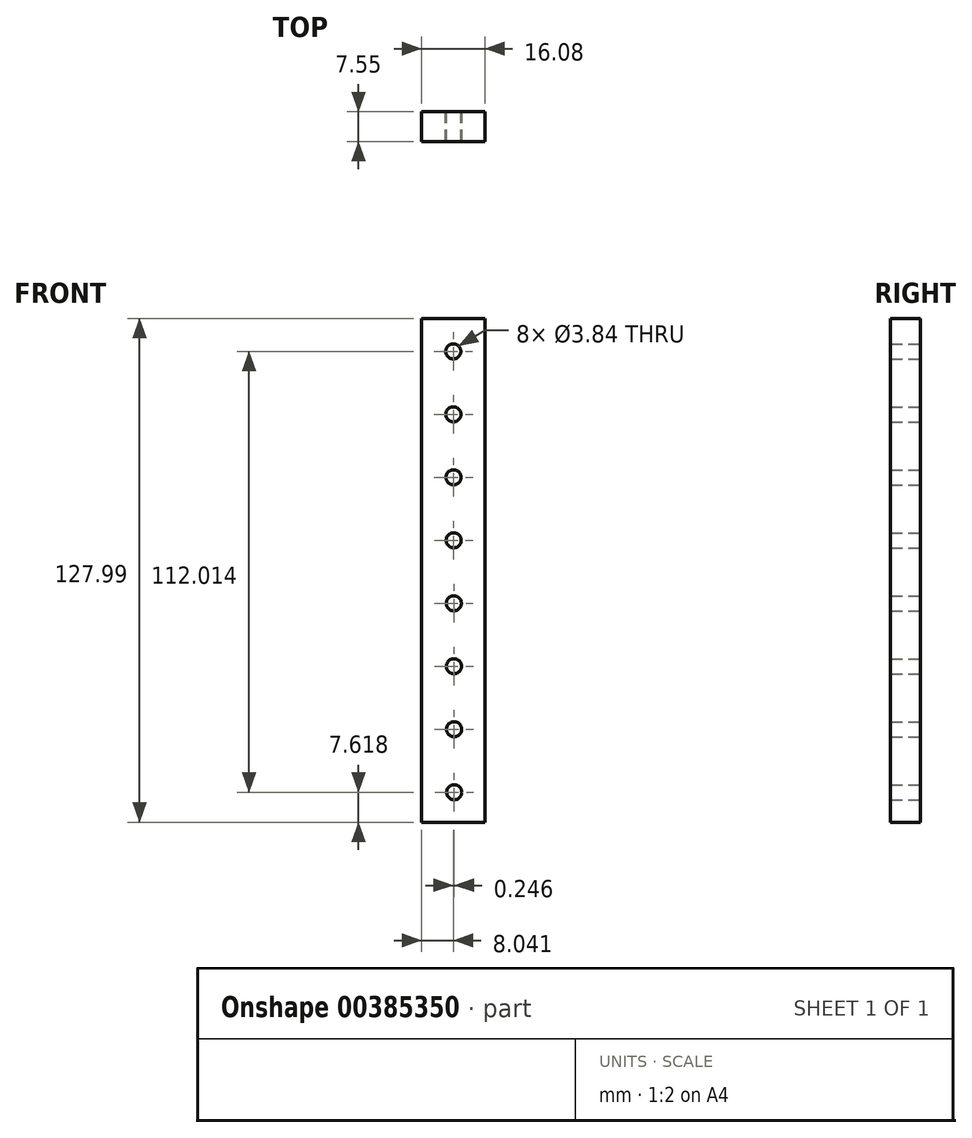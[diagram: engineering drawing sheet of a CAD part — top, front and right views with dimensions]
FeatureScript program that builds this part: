
annotation { "Feature Type Name" : "Feature", "Feature Type Description" : "" }
export const myFeature = defineFeature(function(context is Context, id is Id, definition is map)
    precondition{}
    {
        {
            var Q0;
            Q0=qCreatedBy(makeId("Front.planeOp"),FACE);
            var sketch = newSketch(context, id + "F0", { "sketchPlane" : qUnion([Q0])});
            skLineSegment(sketch, "E0", {"start": v(-32.66, 62.4) * mm, "end": v(-32.66, -65.58) * mm});
            skLineSegment(sketch, "E1", {"start": v(-32.66, -65.58) * mm, "end": v(-16.58, -65.58) * mm});
            skLineSegment(sketch, "E2", {"start": v(-32.66, 62.4) * mm, "end": v(-16.58, 62.4) * mm});
            skLineSegment(sketch, "E3", {"start": v(-16.58, 62.4) * mm, "end": v(-16.58, -65.58) * mm});
            skCircle(sketch, "E4", {"center": v(-24.62, 54.05) * mm, "radius": 1.92 * mm});
            skCircle(sketch, "E5.1.0.0", {"center": v(-24.58, 38.05) * mm, "radius": 1.92 * mm});
            skCircle(sketch, "E5.2.0.0", {"center": v(-24.55, 22.05) * mm, "radius": 1.92 * mm});
            skCircle(sketch, "E5.3.0.0", {"center": v(-24.51, 6.05) * mm, "radius": 1.92 * mm});
            skCircle(sketch, "E5.4.0.0", {"center": v(-24.48, -9.96) * mm, "radius": 1.92 * mm});
            skCircle(sketch, "E5.5.0.0", {"center": v(-24.44, -25.96) * mm, "radius": 1.92 * mm});
            skCircle(sketch, "E5.6.0.0", {"center": v(-24.4, -41.96) * mm, "radius": 1.92 * mm});
            skCircle(sketch, "E5.7.0.0", {"center": v(-24.37, -57.96) * mm, "radius": 1.92 * mm});
            skLineSegment(sketch, "E6", {"start": v(-16.58, 59.8) * mm, "end": v(-32.66, 59.8) * mm});
            skLineSegment(sketch, "E7.1.0.0", {"start": v(-16.58, 57.26) * mm, "end": v(-32.66, 57.26) * mm});
            skLineSegment(sketch, "E7.2.0.0", {"start": v(-16.58, 54.72) * mm, "end": v(-32.66, 54.72) * mm});
            skLineSegment(sketch, "E7.3.0.0", {"start": v(-16.58, 52.18) * mm, "end": v(-32.66, 52.18) * mm});
            skLineSegment(sketch, "E7.4.0.0", {"start": v(-16.58, 49.64) * mm, "end": v(-32.66, 49.64) * mm});
            skLineSegment(sketch, "E7.5.0.0", {"start": v(-16.58, 47.1) * mm, "end": v(-32.66, 47.1) * mm});
            skLineSegment(sketch, "E7.6.0.0", {"start": v(-16.58, 44.56) * mm, "end": v(-32.66, 44.56) * mm});
            skLineSegment(sketch, "E7.7.0.0", {"start": v(-16.58, 42.02) * mm, "end": v(-32.66, 42.02) * mm});
            skLineSegment(sketch, "E7.8.0.0", {"start": v(-16.58, 39.48) * mm, "end": v(-32.66, 39.48) * mm});
            skLineSegment(sketch, "E7.9.0.0", {"start": v(-16.58, 36.94) * mm, "end": v(-32.66, 36.94) * mm});
            skLineSegment(sketch, "E7.10.0.0", {"start": v(-16.58, 34.4) * mm, "end": v(-32.66, 34.4) * mm});
            skLineSegment(sketch, "E7.11.0.0", {"start": v(-16.58, 31.86) * mm, "end": v(-32.66, 31.86) * mm});
            skLineSegment(sketch, "E7.12.0.0", {"start": v(-16.58, 29.32) * mm, "end": v(-32.66, 29.32) * mm});
            skLineSegment(sketch, "E7.13.0.0", {"start": v(-16.58, 26.78) * mm, "end": v(-32.66, 26.78) * mm});
            skLineSegment(sketch, "E7.14.0.0", {"start": v(-16.58, 24.24) * mm, "end": v(-32.66, 24.24) * mm});
            skLineSegment(sketch, "E7.15.0.0", {"start": v(-16.59, 21.7) * mm, "end": v(-32.67, 21.7) * mm});
            skLineSegment(sketch, "E7.16.0.0", {"start": v(-16.59, 19.16) * mm, "end": v(-32.67, 19.16) * mm});
            skLineSegment(sketch, "E7.17.0.0", {"start": v(-16.59, 16.62) * mm, "end": v(-32.67, 16.62) * mm});
            skLineSegment(sketch, "E7.18.0.0", {"start": v(-16.59, 14.08) * mm, "end": v(-32.67, 14.08) * mm});
            skLineSegment(sketch, "E7.19.0.0", {"start": v(-16.59, 11.54) * mm, "end": v(-32.67, 11.54) * mm});
            skLineSegment(sketch, "E7.20.0.0", {"start": v(-16.59, 9) * mm, "end": v(-32.67, 9) * mm});
            skLineSegment(sketch, "E7.21.0.0", {"start": v(-16.59, 6.46) * mm, "end": v(-32.67, 6.46) * mm});
            skLineSegment(sketch, "E7.22.0.0", {"start": v(-16.59, 3.92) * mm, "end": v(-32.67, 3.92) * mm});
            skLineSegment(sketch, "E7.23.0.0", {"start": v(-16.59, 1.38) * mm, "end": v(-32.67, 1.38) * mm});
            skLineSegment(sketch, "E7.24.0.0", {"start": v(-16.59, -1.16) * mm, "end": v(-32.67, -1.16) * mm});
            skLineSegment(sketch, "E7.25.0.0", {"start": v(-16.59, -3.7) * mm, "end": v(-32.67, -3.7) * mm});
            skLineSegment(sketch, "E7.26.0.0", {"start": v(-16.59, -6.24) * mm, "end": v(-32.67, -6.24) * mm});
            skLineSegment(sketch, "E7.27.0.0", {"start": v(-16.59, -8.78) * mm, "end": v(-32.67, -8.78) * mm});
            skLineSegment(sketch, "E7.28.0.0", {"start": v(-16.6, -11.32) * mm, "end": v(-32.67, -11.32) * mm});
            skLineSegment(sketch, "E7.29.0.0", {"start": v(-16.6, -13.86) * mm, "end": v(-32.67, -13.86) * mm});
            skLineSegment(sketch, "E7.30.0.0", {"start": v(-16.6, -16.4) * mm, "end": v(-32.67, -16.4) * mm});
            skLineSegment(sketch, "E7.31.0.0", {"start": v(-16.6, -18.94) * mm, "end": v(-32.67, -18.94) * mm});
            skLineSegment(sketch, "E7.32.0.0", {"start": v(-16.6, -21.48) * mm, "end": v(-32.67, -21.48) * mm});
            skLineSegment(sketch, "E7.33.0.0", {"start": v(-16.6, -24.02) * mm, "end": v(-32.67, -24.02) * mm});
            skLineSegment(sketch, "E7.34.0.0", {"start": v(-16.6, -26.56) * mm, "end": v(-32.67, -26.56) * mm});
            skLineSegment(sketch, "E7.35.0.0", {"start": v(-16.6, -29.1) * mm, "end": v(-32.67, -29.1) * mm});
            skLineSegment(sketch, "E7.36.0.0", {"start": v(-16.6, -31.64) * mm, "end": v(-32.67, -31.64) * mm});
            skLineSegment(sketch, "E7.37.0.0", {"start": v(-16.6, -34.18) * mm, "end": v(-32.67, -34.18) * mm});
            skLineSegment(sketch, "E7.38.0.0", {"start": v(-16.6, -36.72) * mm, "end": v(-32.67, -36.72) * mm});
            skLineSegment(sketch, "E7.39.0.0", {"start": v(-16.6, -39.26) * mm, "end": v(-32.67, -39.26) * mm});
            skLineSegment(sketch, "E7.40.0.0", {"start": v(-16.6, -41.8) * mm, "end": v(-32.67, -41.8) * mm});
            skLineSegment(sketch, "E7.41.0.0", {"start": v(-16.6, -44.34) * mm, "end": v(-32.68, -44.34) * mm});
            skLineSegment(sketch, "E7.42.0.0", {"start": v(-16.6, -46.88) * mm, "end": v(-32.68, -46.88) * mm});
            skLineSegment(sketch, "E7.43.0.0", {"start": v(-16.6, -49.42) * mm, "end": v(-32.68, -49.42) * mm});
            skLineSegment(sketch, "E7.44.0.0", {"start": v(-16.6, -51.96) * mm, "end": v(-32.68, -51.96) * mm});
            skLineSegment(sketch, "E7.45.0.0", {"start": v(-16.6, -54.5) * mm, "end": v(-32.68, -54.5) * mm});
            skLineSegment(sketch, "E7.46.0.0", {"start": v(-16.6, -57.04) * mm, "end": v(-32.68, -57.04) * mm});
            skLineSegment(sketch, "E7.47.0.0", {"start": v(-16.6, -59.58) * mm, "end": v(-32.68, -59.58) * mm});
            skLineSegment(sketch, "E7.48.0.0", {"start": v(-16.6, -62.12) * mm, "end": v(-32.68, -62.12) * mm});
            skLineSegment(sketch, "E7.direction1", {"start": v(-32.66, 59.8) * mm, "end": v(-32.66, 57.26) * mm, "construction": true});
            skSolve(sketch);
        }
        {
            var Q0;
            Q0 = qSketchRegion(id + "F0", true);
            extrude(context, id + "F1", {"entities" : qUnion([Q0]), "depth" : 7.55 * mm});
        }
        {
            var Q0;
            Q0=makeQuery(id+"F1.opExtrude","CAP_FACE",FACE,{"disambiguationData":[OSD([sQuery(id+"F0.wireOp",EDGE,"E0"),sQuery(id+"F0.wireOp",EDGE,"E1"),sQuery(id+"F0.wireOp",EDGE,"E2"),sQuery(id+"F0.wireOp",EDGE,"E3"),sQuery(id+"F0.wireOp",EDGE,"E4"),sQuery(id+"F0.wireOp",EDGE,"E5.1.0.0"),sQuery(id+"F0.wireOp",EDGE,"E5.2.0.0"),sQuery(id+"F0.wireOp",EDGE,"E5.3.0.0"),sQuery(id+"F0.wireOp",EDGE,"E5.4.0.0"),sQuery(id+"F0.wireOp",EDGE,"E5.5.0.0"),sQuery(id+"F0.wireOp",EDGE,"E5.6.0.0"),sQuery(id+"F0.wireOp",EDGE,"E5.7.0.0")])],"isStart":false});
            var sketch = newSketch(context, id + "F2", { "sketchPlane" : qUnion([Q0])});
            skLineSegment(sketch, "E8", {"start": v(-16.58, 58.15) * mm, "end": v(-32.66, 58.15) * mm});
            skLineSegment(sketch, "E9.3.0.0", {"start": v(-16.58, 50.53) * mm, "end": v(-32.66, 50.53) * mm});
            skLineSegment(sketch, "E9.4.0.0", {"start": v(-16.59, 48) * mm, "end": v(-32.67, 48) * mm});
            skLineSegment(sketch, "E9.5.0.0", {"start": v(-16.59, 45.45) * mm, "end": v(-32.67, 45.45) * mm});
            skLineSegment(sketch, "E9.6.0.0", {"start": v(-16.59, 42.91) * mm, "end": v(-32.67, 42.91) * mm});
            skLineSegment(sketch, "E9.7.0.0", {"start": v(-16.6, 40.37) * mm, "end": v(-32.67, 40.37) * mm});
            skLineSegment(sketch, "E9.9.0.0", {"start": v(-16.6, 35.3) * mm, "end": v(-32.67, 35.3) * mm});
            skLineSegment(sketch, "E9.10.0.0", {"start": v(-16.6, 32.75) * mm, "end": v(-32.68, 32.75) * mm});
            skLineSegment(sketch, "E9.11.0.0", {"start": v(-16.6, 30.21) * mm, "end": v(-32.68, 30.21) * mm});
            skLineSegment(sketch, "E9.12.0.0", {"start": v(-16.6, 27.67) * mm, "end": v(-32.68, 27.67) * mm});
            skLineSegment(sketch, "E9.13.0.0", {"start": v(-16.6, 25.13) * mm, "end": v(-32.68, 25.13) * mm});
            skLineSegment(sketch, "E9.15.0.0", {"start": v(-16.6, 20.05) * mm, "end": v(-32.68, 20.05) * mm});
            skLineSegment(sketch, "E9.16.0.0", {"start": v(-16.6, 17.51) * mm, "end": v(-32.68, 17.51) * mm});
            skLineSegment(sketch, "E9.17.0.0", {"start": v(-16.6, 14.97) * mm, "end": v(-32.69, 14.97) * mm});
            skLineSegment(sketch, "E9.18.0.0", {"start": v(-16.6, 12.43) * mm, "end": v(-32.69, 12.43) * mm});
            skLineSegment(sketch, "E9.19.0.0", {"start": v(-16.6, 9.9) * mm, "end": v(-32.69, 9.9) * mm});
            skLineSegment(sketch, "E9.20.0.0", {"start": v(-16.61, 7.35) * mm, "end": v(-23.1, 7.35) * mm});
            skLineSegment(sketch, "E9.22.0.0", {"start": v(-16.61, 2.27) * mm, "end": v(-32.7, 2.27) * mm});
            skLineSegment(sketch, "E9.23.0.0", {"start": v(-16.62, -0.27) * mm, "end": v(-32.7, -0.27) * mm});
            skLineSegment(sketch, "E9.24.0.0", {"start": v(-16.62, -2.8) * mm, "end": v(-32.7, -2.8) * mm});
            skLineSegment(sketch, "E9.25.0.0", {"start": v(-16.62, -5.35) * mm, "end": v(-32.7, -5.35) * mm});
            skLineSegment(sketch, "E9.26.0.0", {"start": v(-16.62, -7.89) * mm, "end": v(-32.7, -7.89) * mm});
            skLineSegment(sketch, "E9.27.0.0", {"start": v(-16.62, -10.43) * mm, "end": v(-22.62, -10.43) * mm});
            skLineSegment(sketch, "E9.28.0.0", {"start": v(-16.62, -12.97) * mm, "end": v(-32.7, -12.97) * mm});
            skLineSegment(sketch, "E9.29.0.0", {"start": v(-16.63, -15.5) * mm, "end": v(-32.7, -15.5) * mm});
            skLineSegment(sketch, "E9.30.0.0", {"start": v(-16.63, -18.05) * mm, "end": v(-32.7, -18.05) * mm});
            skLineSegment(sketch, "E9.31.0.0", {"start": v(-16.63, -20.59) * mm, "end": v(-32.7, -20.59) * mm});
            skLineSegment(sketch, "E9.32.0.0", {"start": v(-16.63, -23.13) * mm, "end": v(-32.71, -23.13) * mm});
            skLineSegment(sketch, "E9.34.0.0", {"start": v(-16.63, -28.2) * mm, "end": v(-32.71, -28.2) * mm});
            skLineSegment(sketch, "E9.35.0.0", {"start": v(-16.63, -30.75) * mm, "end": v(-32.71, -30.75) * mm});
            skLineSegment(sketch, "E9.36.0.0", {"start": v(-16.64, -33.29) * mm, "end": v(-32.72, -33.29) * mm});
            skLineSegment(sketch, "E9.37.0.0", {"start": v(-16.64, -35.83) * mm, "end": v(-32.72, -35.83) * mm});
            skLineSegment(sketch, "E9.38.0.0", {"start": v(-16.64, -38.37) * mm, "end": v(-32.72, -38.37) * mm});
            skLineSegment(sketch, "E9.41.0.0", {"start": v(-16.64, -45.99) * mm, "end": v(-32.72, -45.99) * mm});
            skLineSegment(sketch, "E9.42.0.0", {"start": v(-16.65, -48.53) * mm, "end": v(-32.73, -48.53) * mm});
            skLineSegment(sketch, "E9.43.0.0", {"start": v(-16.65, -51.07) * mm, "end": v(-32.73, -51.07) * mm});
            skLineSegment(sketch, "E9.44.0.0", {"start": v(-16.65, -53.6) * mm, "end": v(-32.73, -53.6) * mm});
            skLineSegment(sketch, "E9.45.0.0", {"start": v(-16.65, -56.15) * mm, "end": v(-32.73, -56.15) * mm});
            skLineSegment(sketch, "E9.47.0.0", {"start": v(-16.65, -61.23) * mm, "end": v(-32.73, -61.23) * mm});
            skLineSegment(sketch, "E9.48.0.0", {"start": v(-16.66, -63.77) * mm, "end": v(-32.74, -63.77) * mm});
            skLineSegment(sketch, "E9.direction1", {"start": v(-32.66, 58.15) * mm, "end": v(-32.66, 55.61) * mm, "construction": true});
            skLineSegment(sketch, "E10", {"start": v(-16.58, 60.16) * mm, "end": v(-32.66, 60.16) * mm});
            skLineSegment(sketch, "E11.trimOffspring", {"start": v(-26.34, -10.43) * mm, "end": v(-32.7, -10.43) * mm});
            skLineSegment(sketch, "E12.trimOffspring", {"start": v(-25.92, 7.35) * mm, "end": v(-32.7, 7.35) * mm});
            skLineSegment(sketch, "E13", {"start": v(-32.66, -58.37) * mm, "end": v(-26.25, -58.37) * mm});
            skLineSegment(sketch, "E14", {"start": v(-22.48, -58.3) * mm, "end": v(-16.58, -58.3) * mm});
            skLineSegment(sketch, "E15", {"start": v(-16.58, -43.5) * mm, "end": v(-23.27, -43.5) * mm});
            skLineSegment(sketch, "E16", {"start": v(-25.58, -43.48) * mm, "end": v(-32.72, -43.48) * mm});
            skPoint(sketch, "E17.start.orphan", {"position": v(-32.72, -43.48) * mm});
            skLineSegment(sketch, "E18", {"start": v(-32.66, -41.1) * mm, "end": v(-26.13, -41.1) * mm});
            skLineSegment(sketch, "E19", {"start": v(-22.67, -41.15) * mm, "end": v(-16.58, -41.15) * mm});
            skLineSegment(sketch, "E20", {"start": v(-32.66, -25.68) * mm, "end": v(-26.34, -25.68) * mm});
            skLineSegment(sketch, "E21", {"start": v(-22.54, -25.75) * mm, "end": v(-16.58, -25.75) * mm});
            skLineSegment(sketch, "E22", {"start": v(-32.66, 22.38) * mm, "end": v(-26.44, 22.38) * mm});
            skLineSegment(sketch, "E23", {"start": v(-22.66, 22.37) * mm, "end": v(-16.58, 22.37) * mm});
            skLineSegment(sketch, "E24", {"start": v(-32.66, 37.67) * mm, "end": v(-26.47, 37.67) * mm});
            skLineSegment(sketch, "E25", {"start": v(-22.7, 37.7) * mm, "end": v(-16.6, 37.7) * mm});
            skLineSegment(sketch, "E26", {"start": v(-32.66, 55.61) * mm, "end": v(-25.74, 55.6) * mm});
            skLineSegment(sketch, "E27", {"start": v(-23.39, 55.53) * mm, "end": v(-16.58, 55.53) * mm});
            skLineSegment(sketch, "E28", {"start": v(-32.66, 52.92) * mm, "end": v(-26.17, 52.92) * mm});
            skLineSegment(sketch, "E29", {"start": v(-23.03, 52.97) * mm, "end": v(-16.58, 52.97) * mm});
            skLineSegment(sketch, "E30", {"start": v(-32.66, 4.98) * mm, "end": v(-26.1, 4.98) * mm});
            skLineSegment(sketch, "E31", {"start": v(-22.94, 4.94) * mm, "end": v(-16.58, 4.94) * mm});
            skSolve(sketch);
        }
        {
            var Q0;
            Q0=sQuery(id+"F2.wireOp",EDGE,"E10");
            var Q1;
            Q1=sQuery(id+"F2.wireOp",EDGE,"E8");
            var Q2;
            Q2=sQuery(id+"F2.wireOp",EDGE,"E9.3.0.0");
            var Q3;
            Q3=sQuery(id+"F2.wireOp",EDGE,"E9.4.0.0");
            var Q4;
            Q4=sQuery(id+"F2.wireOp",EDGE,"E9.5.0.0");
            var Q5;
            Q5=sQuery(id+"F2.wireOp",EDGE,"E9.6.0.0");
            var Q6;
            Q6=sQuery(id+"F2.wireOp",EDGE,"E9.7.0.0");
            var Q7;
            Q7=sQuery(id+"F2.wireOp",EDGE,"E9.9.0.0");
            var Q8;
            Q8=sQuery(id+"F2.wireOp",EDGE,"E9.10.0.0");
            var Q9;
            Q9=sQuery(id+"F2.wireOp",EDGE,"E9.11.0.0");
            var Q10;
            Q10=sQuery(id+"F2.wireOp",EDGE,"E9.12.0.0");
            var Q11;
            Q11=sQuery(id+"F2.wireOp",EDGE,"E9.13.0.0");
            var Q12;
            Q12=sQuery(id+"F2.wireOp",EDGE,"E9.15.0.0");
            var Q13;
            Q13=sQuery(id+"F2.wireOp",EDGE,"E9.16.0.0");
            var Q14;
            Q14=sQuery(id+"F2.wireOp",EDGE,"E9.17.0.0");
            var Q15;
            Q15=sQuery(id+"F2.wireOp",EDGE,"E9.18.0.0");
            var Q16;
            Q16=sQuery(id+"F2.wireOp",EDGE,"E9.19.0.0");
            var Q17;
            Q17=sQuery(id+"F2.wireOp",EDGE,"E9.20.0.0");
            var Q18;
            Q18=sQuery(id+"F2.wireOp",EDGE,"E9.22.0.0");
            var Q19;
            Q19=sQuery(id+"F2.wireOp",EDGE,"E9.23.0.0");
            var Q20;
            Q20=sQuery(id+"F2.wireOp",EDGE,"E9.24.0.0");
            var Q21;
            Q21=sQuery(id+"F2.wireOp",EDGE,"E9.25.0.0");
            var Q22;
            Q22=sQuery(id+"F2.wireOp",EDGE,"E9.27.0.0");
            var Q23;
            Q23=sQuery(id+"F2.wireOp",EDGE,"E9.26.0.0");
            var Q24;
            Q24=sQuery(id+"F2.wireOp",EDGE,"E9.28.0.0");
            var Q25;
            Q25=sQuery(id+"F2.wireOp",EDGE,"E9.29.0.0");
            var Q26;
            Q26=sQuery(id+"F2.wireOp",EDGE,"E9.31.0.0");
            var Q27;
            Q27=sQuery(id+"F2.wireOp",EDGE,"E9.30.0.0");
            var Q28;
            Q28=sQuery(id+"F2.wireOp",EDGE,"E9.32.0.0");
            var Q29;
            Q29=sQuery(id+"F2.wireOp",EDGE,"E9.34.0.0");
            var Q30;
            Q30=sQuery(id+"F2.wireOp",EDGE,"E9.35.0.0");
            var Q31;
            Q31=sQuery(id+"F2.wireOp",EDGE,"E9.36.0.0");
            var Q32;
            Q32=sQuery(id+"F2.wireOp",EDGE,"E9.37.0.0");
            var Q33;
            Q33=sQuery(id+"F2.wireOp",EDGE,"E9.38.0.0");
            var Q34;
            Q34=sQuery(id+"F2.wireOp",EDGE,"E9.41.0.0");
            var Q35;
            Q35=sQuery(id+"F2.wireOp",EDGE,"E9.42.0.0");
            var Q36;
            Q36=sQuery(id+"F2.wireOp",EDGE,"E9.43.0.0");
            var Q37;
            Q37=sQuery(id+"F2.wireOp",EDGE,"E9.44.0.0");
            var Q38;
            Q38=sQuery(id+"F2.wireOp",EDGE,"E9.45.0.0");
            var Q39;
            Q39=sQuery(id+"F2.wireOp",EDGE,"E9.47.0.0");
            var Q40;
            Q40=sQuery(id+"F2.wireOp",EDGE,"E9.48.0.0");
            var Q41;
            Q41=sQuery(id+"F2.wireOp",EDGE,"E22");
            var Q42;
            Q42=sQuery(id+"F2.wireOp",EDGE,"E23");
            var Q43;
            Q43=sQuery(id+"F2.wireOp",EDGE,"E24");
            var Q44;
            Q44=sQuery(id+"F2.wireOp",EDGE,"E25");
            var Q45;
            Q45=sQuery(id+"F2.wireOp",EDGE,"E28");
            var Q46;
            Q46=sQuery(id+"F2.wireOp",EDGE,"E29");
            var Q47;
            Q47=sQuery(id+"F2.wireOp",EDGE,"E27");
            var Q48;
            Q48=sQuery(id+"F2.wireOp",EDGE,"E26");
            var Q49;
            Q49=sQuery(id+"F2.wireOp",EDGE,"E12.trimOffspring");
            var Q50;
            Q50=sQuery(id+"F2.wireOp",EDGE,"E11.trimOffspring");
            var Q51;
            Q51=sQuery(id+"F2.wireOp",EDGE,"E20");
            var Q52;
            Q52=sQuery(id+"F2.wireOp",EDGE,"E21");
            var Q53;
            Q53=sQuery(id+"F2.wireOp",EDGE,"E18");
            var Q54;
            Q54=sQuery(id+"F2.wireOp",EDGE,"E19");
            var Q55;
            Q55=sQuery(id+"F2.wireOp",EDGE,"E15");
            var Q56;
            Q56=sQuery(id+"F2.wireOp",EDGE,"E16");
            var Q57;
            Q57=sQuery(id+"F2.wireOp",EDGE,"E13");
            var Q58;
            Q58=sQuery(id+"F2.wireOp",EDGE,"E14");
            var Q59;
            Q59=sQuery(id+"F2.wireOp",EDGE,"E30");
            var Q60;
            Q60=sQuery(id+"F2.wireOp",EDGE,"E31");
            extrude(context, id + "F3", {"bodyType" : ToolBodyType.SURFACE, "surfaceEntities" : qUnion([Q0, Q1, Q2, Q3, Q4, Q5, Q6, Q7, Q8, Q9, Q10, Q11, Q12, Q13, Q14, Q15, Q16, Q17, Q18, Q19, Q20, Q21, Q22, Q23, Q24, Q25, Q26, Q27, Q28, Q29, Q30, Q31, Q32, Q33, Q34, Q35, Q36, Q37, Q38, Q39, Q40, Q41, Q42, Q43, Q44, Q45, Q46, Q47, Q48, Q49, Q50, Q51, Q52, Q53, Q54, Q55, Q56, Q57, Q58, Q59, Q60]), "oppositeDirection" : true, "depth" : 2.54 * mm});
        }
    });
